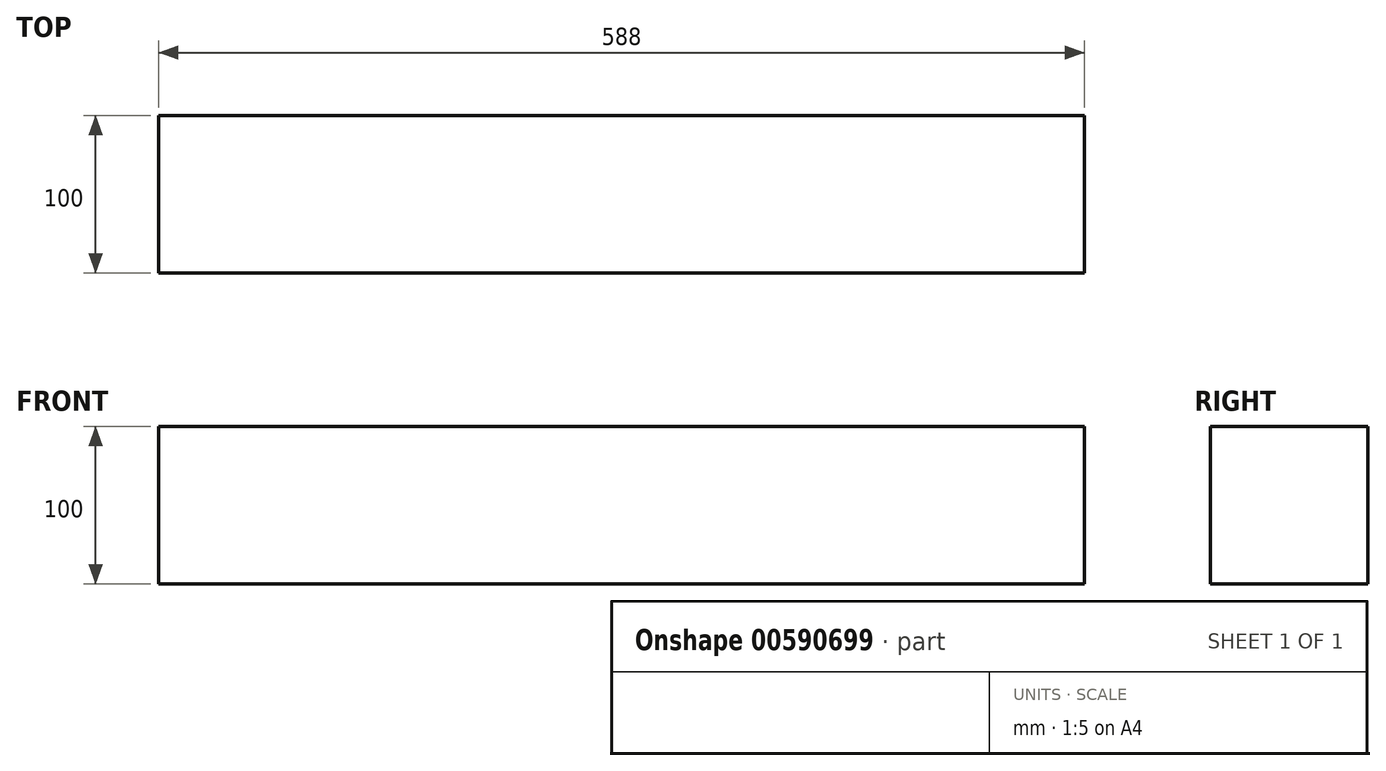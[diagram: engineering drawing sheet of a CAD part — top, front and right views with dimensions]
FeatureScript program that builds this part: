
annotation { "Feature Type Name" : "Feature", "Feature Type Description" : "" }
export const myFeature = defineFeature(function(context is Context, id is Id, definition is map)
    precondition{}
    {
        {
            assignVariable(context, id + "F0", {"name" : "longueur", "anyValue" : 100});
        }
        {
            var Q0;
            Q0=qCreatedBy(makeId("Front.planeOp"),FACE);
            var sketch = newSketch(context, id + "F1", { "sketchPlane" : qUnion([Q0])});
            skLineSegment(sketch, "E0.bottom", {"start": v(-294, 50) * mm, "end": v(294, 50) * mm});
            skLineSegment(sketch, "E0.top", {"start": v(-294, -50) * mm, "end": v(294, -50) * mm});
            skLineSegment(sketch, "E0.left", {"start": v(-294, 50) * mm, "end": v(-294, -50) * mm});
            skLineSegment(sketch, "E0.right", {"start": v(294, 50) * mm, "end": v(294, -50) * mm});
            skPoint(sketch, "E0.middle", {"position": v(0, 0) * mm});
            skSolve(sketch);
        }
        {
            var Q0;
            Q0=qSketchRegion(id+"F1",true);
            extrude(context, id + "F2", {"entities" : qUnion([Q0]), "endBound" : BoundingType.SYMMETRIC, "depth" : (getVariable(context, 'longueur')) * mm, "offsetDistance" : 25 * mm});
        }
    });
